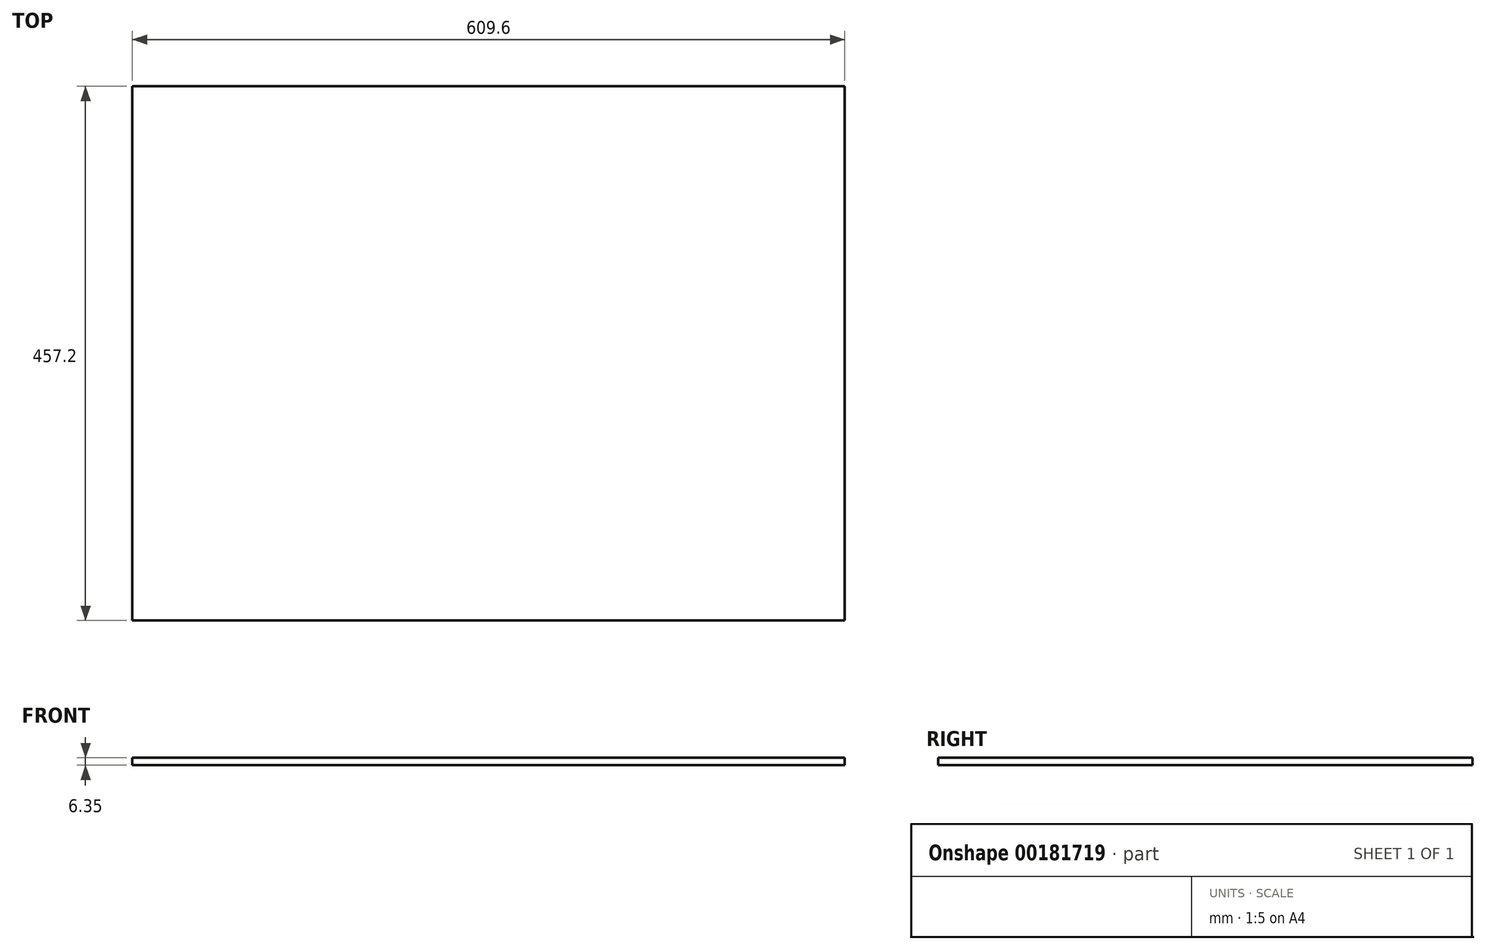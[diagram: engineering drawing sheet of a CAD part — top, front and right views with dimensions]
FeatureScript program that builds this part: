
annotation { "Feature Type Name" : "Feature", "Feature Type Description" : "" }
export const myFeature = defineFeature(function(context is Context, id is Id, definition is map)
    precondition{}
    {
        {
            var Q0;
            Q0=qCreatedBy(makeId("Top.planeOp"),FACE);
            var sketch = newSketch(context, id + "F0", { "sketchPlane" : qUnion([Q0])});
            skLineSegment(sketch, "E0.bottom", {"start": v(-312.49, -241.56) * mm, "end": v(297.11, -241.56) * mm});
            skLineSegment(sketch, "E0.top", {"start": v(-312.49, 215.64) * mm, "end": v(297.11, 215.64) * mm});
            skLineSegment(sketch, "E0.left", {"start": v(-312.49, -241.56) * mm, "end": v(-312.49, 215.64) * mm});
            skLineSegment(sketch, "E0.right", {"start": v(297.11, -241.56) * mm, "end": v(297.11, 215.64) * mm});
            skSolve(sketch);
        }
        {
            var Q0;
            Q0=makeQuery(id+"F0.imprint","IMPRINT",FACE,{"disambiguationData":[TD([[makeQuery(id+"F0.imprint","IMPRINT",EDGE,{"derivedFrom":sQuery(id+"F0.wireOp",EDGE,"E0.bottom")}),1.0]])]});
            extrude(context, id + "F1", {"entities" : qUnion([Q0]), "depth" : 6.35 * mm});
        }
    });
